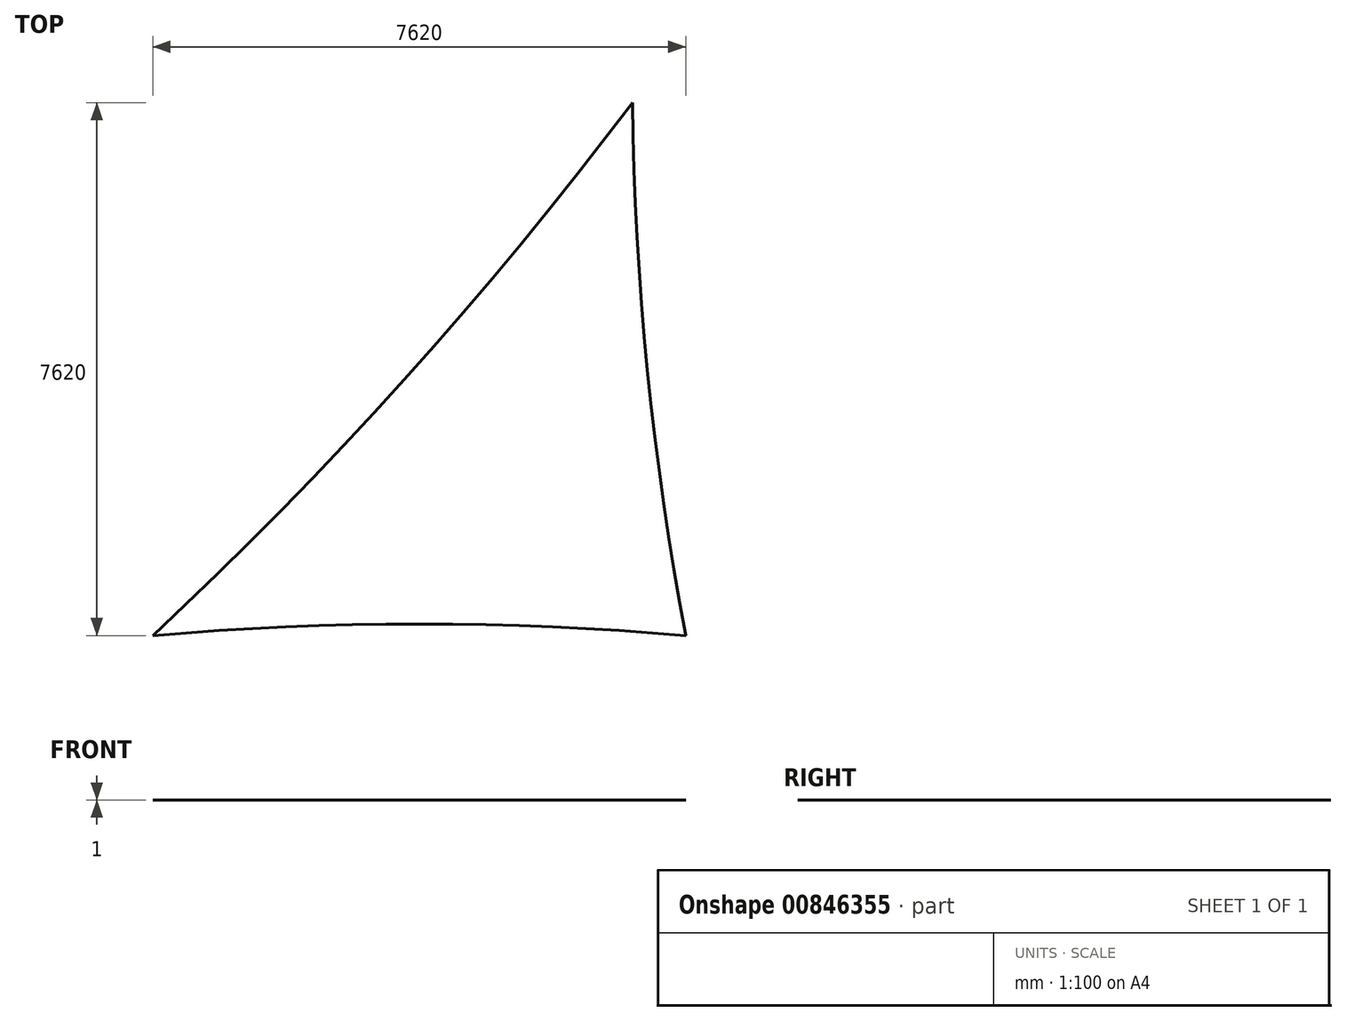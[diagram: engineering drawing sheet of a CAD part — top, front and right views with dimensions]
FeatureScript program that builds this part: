
annotation { "Feature Type Name" : "Feature", "Feature Type Description" : "" }
export const myFeature = defineFeature(function(context is Context, id is Id, definition is map)
    precondition{}
    {
        {
            var Q0;
            Q0=qCreatedBy(makeId("Top.planeOp"),FACE);
            var sketch = newSketch(context, id + "F0", { "sketchPlane" : qUnion([Q0])});
            skLineSegment(sketch, "E0", {"start": v(-762, 7620) * mm, "end": v(-7620, 0) * mm});
            skLineSegment(sketch, "E1", {"start": v(-7620, 0) * mm, "end": v(0, 0) * mm});
            skLineSegment(sketch, "E2", {"start": v(0, 0) * mm, "end": v(-762, 7620) * mm});
            skArc(sketch, "E3", {"start": v(-7620, 0) * mm, "mid": v(-4024.65, 3660.29) * mm, "end": v(-762, 7620) * mm});
            skArc(sketch, "E4", {"start": v(-762, 7620) * mm, "mid": v(-547.35, 3793.37) * mm, "end": v(0, 0) * mm});
            skArc(sketch, "E5", {"start": v(0, 0) * mm, "mid": v(-3810, 166.35) * mm, "end": v(-7620, 0) * mm});
            skLineSegment(sketch, "E6", {"start": v(-762, 7620) * mm, "end": v(0, 8631.68) * mm});
            skLineSegment(sketch, "E7", {"start": v(0, 0) * mm, "end": v(37.98, -200.8) * mm});
            skLineSegment(sketch, "E8", {"start": v(-7620, 0) * mm, "end": v(-7917.52, -26.03) * mm});
            skSolve(sketch);
        }
        {
            var Q0;
            Q0=makeQuery(id+"F0.imprint","IMPRINT",FACE,{"disambiguationData":[TD([[makeQuery(id+"F0.imprint","IMPRINT",EDGE,{"derivedFrom":sQuery(id+"F0.wireOp",EDGE,"E3")}),-1.0]])]});
            extrude(context, id + "F1", {"entities" : qUnion([Q0]), "depth" : 1 * mm, "offsetDistance" : 25 * mm});
        }
        {
            var Q0;
            Q0=makeQuery(id+"F1.opExtrude","CAP_FACE",FACE,{"disambiguationData":[OSD([sQuery(id+"F0.wireOp",EDGE,"E3"),sQuery(id+"F0.wireOp",EDGE,"E4"),sQuery(id+"F0.wireOp",EDGE,"E5")])],"isStart":false});
            var sketch = newSketch(context, id + "F2", { "sketchPlane" : qUnion([Q0])});
            skLineSegment(sketch, "E9", {"start": v(-7620, 0) * mm, "end": v(-8157.2, -288.13) * mm});
            skLineSegment(sketch, "E10", {"start": v(0, 0) * mm, "end": v(450.98, -410.15) * mm});
            skLineSegment(sketch, "E11", {"start": v(-762, 7620) * mm, "end": v(-531.26, 8184.25) * mm});
            skLineSegment(sketch, "E12", {"start": v(-7620, 0) * mm, "end": v(-547.35, 3793.37) * mm, "construction": true});
            skLineSegment(sketch, "E13", {"start": v(-4024.65, 3660.29) * mm, "end": v(0, 0) * mm, "construction": true});
            skLineSegment(sketch, "E14", {"start": v(-3810, 166.35) * mm, "end": v(-762, 7620) * mm, "construction": true});
            skSolve(sketch);
        }
    });
